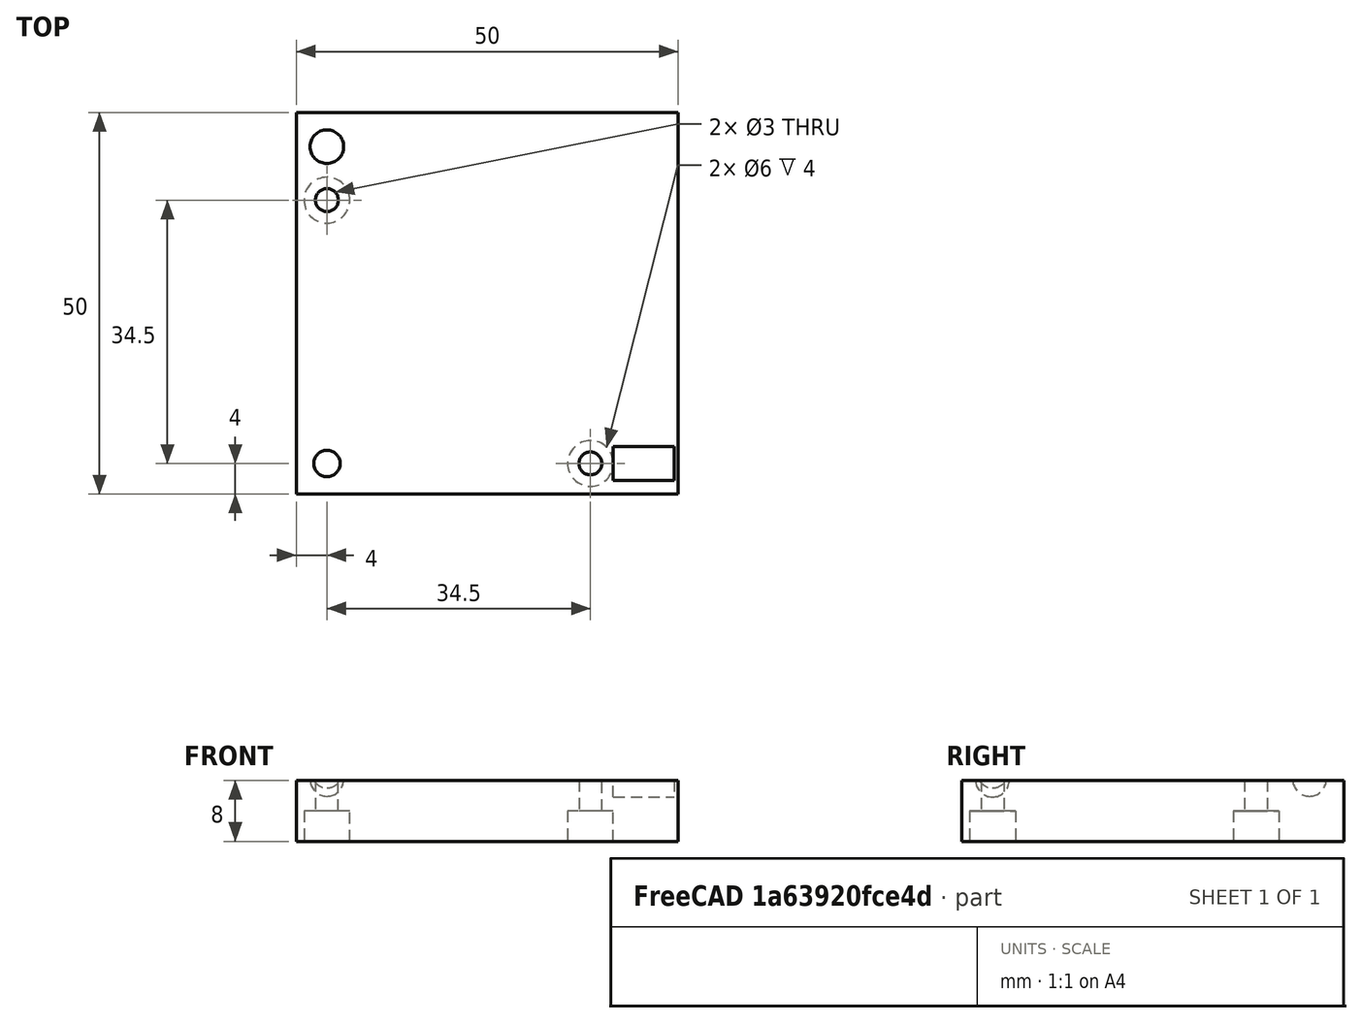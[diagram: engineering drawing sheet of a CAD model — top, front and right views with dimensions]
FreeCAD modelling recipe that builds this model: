
FCSTD DOCUMENT  (FreeCAD 0.21R33668 +7 (Git))
Label: KinematicMountBaseplate_M4
License: All rights reserved
LicenseURL: https://en.wikipedia.org/wiki/All_rights_reserved
objects: Part::Cylinder×5, Part::Cut×5, Part::MultiFuse×2, Part::Sphere×2, Part::Box×1, Spreadsheet::Sheet×1
note: 15 computed .brp shape members not serialized (recipe doc carries the construction recipe); baked Part::Feature solids carry a one-line shape summary decoded from their .brp

FEATURE [Part::Box] Box002  label="Cube002"
  AttacherType = Attacher::AttachEngine3D
  Height = 8
  Length = 50
  Width = 50
  expr: Height = <<MountConfiguration>>.thickness
  expr: Length = <<MountConfiguration>>.outer_length
  expr: Width = <<MountConfiguration>>.outer_length
FEATURE [Part::Cylinder] Cylinder008
  Angle = 360
  AttacherType = Attacher::AttachEngine3D
  FirstAngle = 0
  Height = 8
  Radius = 1.5
  SecondAngle = 0
  expr: Height = <<MountConfiguration>>.thickness
FEATURE [Part::Cylinder] Cylinder009
  Angle = 360
  AttacherType = Attacher::AttachEngine3D
  FirstAngle = 0
  Height = 4
  Radius = 3
  SecondAngle = 0
  expr: Height = <<MountConfiguration>>.thickness / 2
FEATURE [Part::Cylinder] Cylinder010
  Angle = 360
  AttacherType = Attacher::AttachEngine3D
  FirstAngle = 0
  Height = 8
  Radius = 1.5
  SecondAngle = 0
  expr: Height = <<MountConfiguration>>.thickness
FEATURE [Part::Cylinder] Cylinder011
  Angle = 360
  AttacherType = Attacher::AttachEngine3D
  FirstAngle = 0
  Height = 4
  Radius = 3
  SecondAngle = 0
  expr: Height = <<MountConfiguration>>.thickness / 2
FEATURE [Part::Cylinder] Cylinder012
  Angle = 360
  AttacherType = Attacher::AttachEngine3D
  FirstAngle = 0
  Height = 8
  Placement = pos=(41.5,4,8) rot=(0,1,0;1.5708rad)
  Radius = 2.2
  SecondAngle = 0
  expr: .Placement.Base.x = <<MountConfiguration>>.outer_length - 7 / 2 - 1 - 4
  expr: .Placement.Base.y = <<MountConfiguration>>.holder_width / 2
  expr: .Placement.Base.z = <<MountConfiguration>>.thickness
FEATURE [Part::MultiFuse] Fusion004  label="SpringHole003"
  Placement = pos=(38.5,4,0) rot=(0,0,1;0rad)
  Shapes = -> [Cylinder008,Cylinder009]
  expr: .Placement.Base.x = <<MountConfiguration>>.outer_length - 7 / 2 - 1 - 1 * 7
  expr: .Placement.Base.y = <<MountConfiguration>>.holder_width / 2
FEATURE [Part::Cut] Cut008
  Base = -> Box002
  Tool = -> Fusion004
FEATURE [Part::MultiFuse] Fusion005  label="SpringHole004"
  Placement = pos=(4,38.5,0) rot=(0,0,1;0rad)
  Shapes = -> [Cylinder010,Cylinder011]
  expr: .Placement.Base.x = <<MountConfiguration>>.holder_width / 2
  expr: .Placement.Base.y = <<MountConfiguration>>.outer_length - 7 / 2 - 1 - 1 * 7
FEATURE [Part::Cut] Cut009
  Base = -> Cut008
  Tool = -> Fusion005
FEATURE [Part::Sphere] Sphere001
  Angle1 = -90
  Angle2 = 90
  Angle3 = 360
  AttacherType = Attacher::AttachEngine3D
  Placement = pos=(4,4,9) rot=(0,0,1;0rad)
  Radius = 2
  expr: .Placement.Base.x = <<MountConfiguration>>.holder_width / 2
  expr: .Placement.Base.y = <<MountConfiguration>>.holder_width / 2
  expr: .Placement.Base.z = <<MountConfiguration>>.thickness + 1
FEATURE [Part::Cut] Cut010
  Base = -> Cut009
  Tool = -> Sphere001
FEATURE [Part::Sphere] Sphere003
  Angle1 = -90
  Angle2 = 90
  Angle3 = 360
  AttacherType = Attacher::AttachEngine3D
  Placement = pos=(4,45.5,8.1) rot=(0,0,1;0rad)
  Radius = 2.2
  expr: .Placement.Base.x = <<MountConfiguration>>.holder_width / 2
  expr: .Placement.Base.y = <<MountConfiguration>>.outer_length - 7 / 2 - 1
  expr: .Placement.Base.z = <<MountConfiguration>>.thickness + 0.1
FEATURE [Part::Cut] Cut011
  Base = -> Cut010
  Tool = -> Sphere003
FEATURE [Part::Cut] Cut012
  Base = -> Cut011
  Tool = -> Cylinder012
FEATURE [Spreadsheet::Sheet] Spreadsheet  label="MountConfiguration"
  cells = A2='Outer length; B2(outer_length)=50; A3='Holder width; B3(holder_width)=8; A4='Thickness; B4(thickness)=8
